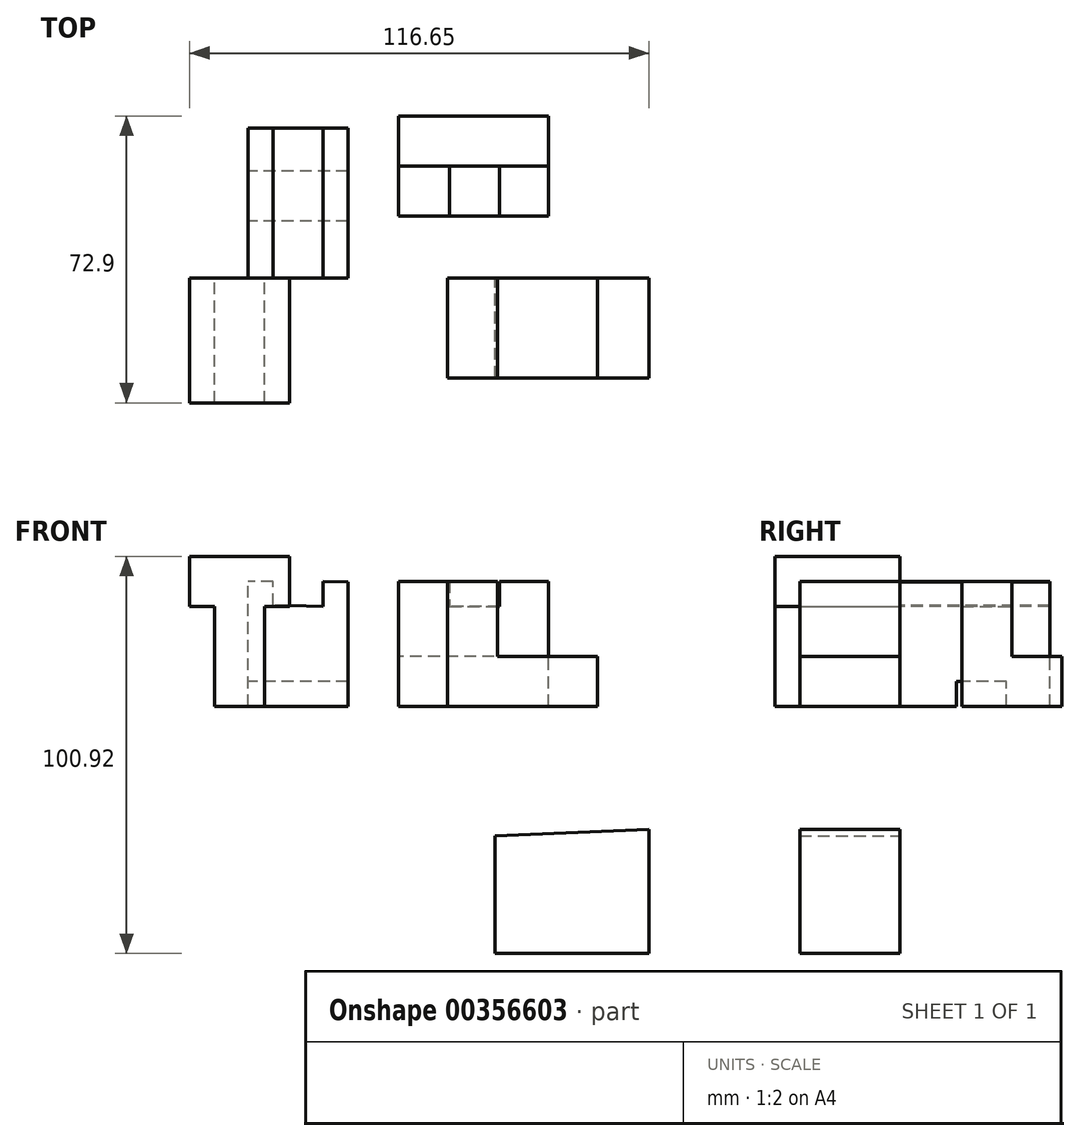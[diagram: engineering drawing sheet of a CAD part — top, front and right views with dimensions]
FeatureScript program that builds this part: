
annotation { "Feature Type Name" : "Feature", "Feature Type Description" : "" }
export const myFeature = defineFeature(function(context is Context, id is Id, definition is map)
    precondition{}
    {
        {
            var Q0;
            Q0=qCreatedBy(makeId("Front.planeOp"),FACE);
            var sketch = newSketch(context, id + "F0", { "sketchPlane" : qUnion([Q0])});
            skLineSegment(sketch, "E0", {"start": v(12.43, 31.75) * mm, "end": v(12.43, 0) * mm});
            skLineSegment(sketch, "E1", {"start": v(12.43, 0) * mm, "end": v(50.53, 0) * mm});
            skLineSegment(sketch, "E2", {"start": v(50.53, 0) * mm, "end": v(50.53, 12.7) * mm});
            skLineSegment(sketch, "E3", {"start": v(50.53, 12.7) * mm, "end": v(25.13, 12.7) * mm});
            skLineSegment(sketch, "E4", {"start": v(25.13, 12.7) * mm, "end": v(25.13, 31.75) * mm});
            skLineSegment(sketch, "E5", {"start": v(25.13, 31.75) * mm, "end": v(12.43, 31.75) * mm});
            skSolve(sketch);
        }
        {
            var Q0;
            Q0 = qSketchRegion(id + "F0", true);
            extrude(context, id + "F1", {"entities" : qUnion([Q0]), "depth" : 25.4 * mm});
        }
        {
            var Q0;
            Q0=qCreatedBy(makeId("Front.planeOp"),FACE);
            var sketch = newSketch(context, id + "F2", { "sketchPlane" : qUnion([Q0])});
            skLineSegment(sketch, "E6", {"start": v(-53.06, 38.1) * mm, "end": v(-53.06, 25.4) * mm});
            skLineSegment(sketch, "E7", {"start": v(-53.06, 25.4) * mm, "end": v(-46.7, 25.4) * mm});
            skLineSegment(sketch, "E8", {"start": v(-46.7, 25.4) * mm, "end": v(-46.7, 0) * mm});
            skLineSegment(sketch, "E9", {"start": v(-46.7, 0) * mm, "end": v(-34, 0) * mm});
            skLineSegment(sketch, "E10", {"start": v(-34, 0) * mm, "end": v(-34, 25.4) * mm});
            skLineSegment(sketch, "E11", {"start": v(-34, 25.4) * mm, "end": v(-27.66, 25.4) * mm});
            skLineSegment(sketch, "E12", {"start": v(-27.66, 25.4) * mm, "end": v(-27.66, 38.1) * mm});
            skLineSegment(sketch, "E13", {"start": v(-27.66, 38.1) * mm, "end": v(-53.06, 38.1) * mm});
            skSolve(sketch);
        }
        {
            var Q0;
            Q0 = qSketchRegion(id + "F2", true);
            extrude(context, id + "F3", {"entities" : qUnion([Q0]), "depth" : 31.75 * mm});
        }
        {
            var Q0;
            Q0=qCreatedBy(makeId("Right.planeOp"),FACE);
            var sketch = newSketch(context, id + "F4", { "sketchPlane" : qUnion([Q0])});
            skLineSegment(sketch, "E14", {"start": v(15.75, 0) * mm, "end": v(15.75, 31.75) * mm});
            skLineSegment(sketch, "E15", {"start": v(15.75, 31.75) * mm, "end": v(28.45, 31.75) * mm});
            skLineSegment(sketch, "E16", {"start": v(28.45, 31.75) * mm, "end": v(28.45, 12.7) * mm});
            skLineSegment(sketch, "E17", {"start": v(28.45, 12.7) * mm, "end": v(41.15, 12.7) * mm});
            skLineSegment(sketch, "E18", {"start": v(41.15, 12.7) * mm, "end": v(41.15, 0) * mm});
            skLineSegment(sketch, "E19", {"start": v(41.15, 0) * mm, "end": v(15.75, 0) * mm});
            skSolve(sketch);
        }
        {
            var Q0;
            Q0 = qSketchRegion(id + "F4", true);
            extrude(context, id + "F5", {"entities" : qUnion([Q0]), "depth" : 38.1 * mm});
        }
        {
            var Q0;
            Q0=makeQuery(id+"F5.opExtrude","SWEPT_FACE",FACE,{"disambiguationData":[OSD([sQuery(id+"F4.wireOp",EDGE,"E16")])]});
            var sketch = newSketch(context, id + "F6", { "sketchPlane" : qUnion([Q0])});
            skLineSegment(sketch, "E20", {"start": v(-25.68, 31.75) * mm, "end": v(-25.68, 25.4) * mm});
            skLineSegment(sketch, "E21", {"start": v(-25.68, 25.4) * mm, "end": v(-12.98, 25.4) * mm});
            skLineSegment(sketch, "E22", {"start": v(-12.98, 25.4) * mm, "end": v(-12.98, 31.75) * mm});
            skLineSegment(sketch, "E23", {"start": v(-25.68, 31.75) * mm, "end": v(-12.98, 31.75) * mm});
            skSolve(sketch);
        }
        {
            var Q0;
            Q0 = qSketchRegion(id + "F6", true);
            extrude(context, id + "F7", {"entities" : qUnion([Q0]), "operationType" : NewBodyOperationType.REMOVE, "oppositeDirection" : true, "depth" : 25.4 * mm});
        }
        {
            var Q0;
            Q0=qCreatedBy(makeId("Front.planeOp"),FACE);
            var sketch = newSketch(context, id + "F8", { "sketchPlane" : qUnion([Q0])});
            skLineSegment(sketch, "E24", {"start": v(-12.87, 0) * mm, "end": v(-38.27, 0) * mm});
            skLineSegment(sketch, "E25", {"start": v(-38.27, 0) * mm, "end": v(-38.27, 31.75) * mm});
            skLineSegment(sketch, "E26", {"start": v(-12.87, 0) * mm, "end": v(-12.87, 31.61) * mm});
            skLineSegment(sketch, "E27", {"start": v(-12.87, 31.61) * mm, "end": v(-19.22, 31.75) * mm});
            skLineSegment(sketch, "E28", {"start": v(-19.22, 31.75) * mm, "end": v(-19.22, 31.55) * mm});
            skLineSegment(sketch, "E29", {"start": v(-31.92, 31.75) * mm, "end": v(-31.92, 31.82) * mm});
            skLineSegment(sketch, "E30", {"start": v(-31.92, 31.75) * mm, "end": v(-38.27, 31.75) * mm});
            skLineSegment(sketch, "E31", {"start": v(-19.22, 31.75) * mm, "end": v(-19.22, 25.4) * mm});
            skLineSegment(sketch, "E32", {"start": v(-19.22, 25.4) * mm, "end": v(-31.91, 25.67) * mm});
            skLineSegment(sketch, "E33", {"start": v(-31.91, 25.67) * mm, "end": v(-31.92, 31.75) * mm});
            skSolve(sketch);
        }
        {
            var Q0;
            Q0 = qSketchRegion(id + "F8", true);
            extrude(context, id + "F9", {"entities" : qUnion([Q0]), "operationType" : NewBodyOperationType.ADD, "oppositeDirection" : true, "depth" : 38.1 * mm});
        }
        {
            var Q0;
            Q0=makeQuery(id+"F9.opExtrude","SWEPT_FACE",FACE,{"disambiguationData":[OSD([sQuery(id+"F8.wireOp",EDGE,"E25")])]});
            var sketch = newSketch(context, id + "F10", { "sketchPlane" : qUnion([Q0])});
            skLineSegment(sketch, "E34.bottom", {"start": v(-27.1, 0) * mm, "end": v(-14.4, 0) * mm});
            skLineSegment(sketch, "E34.top", {"start": v(-27.1, 6.35) * mm, "end": v(-14.4, 6.35) * mm});
            skLineSegment(sketch, "E34.left", {"start": v(-27.1, 0) * mm, "end": v(-27.1, 6.35) * mm});
            skLineSegment(sketch, "E34.right", {"start": v(-14.4, 0) * mm, "end": v(-14.4, 6.35) * mm});
            skSolve(sketch);
        }
        {
            var Q0;
            Q0 = qSketchRegion(id + "F10", true);
            extrude(context, id + "F11", {"entities" : qUnion([Q0]), "operationType" : NewBodyOperationType.REMOVE, "oppositeDirection" : true, "depth" : 25.4 * mm});
        }
        {
            var Q0;
            Q0=qCreatedBy(makeId("Front.planeOp"),FACE);
            var sketch = newSketch(context, id + "F12", { "sketchPlane" : qUnion([Q0])});
            skLineSegment(sketch, "E35", {"start": v(24.55, -32.91) * mm, "end": v(24.55, -62.82) * mm});
            skLineSegment(sketch, "E36", {"start": v(24.55, -62.82) * mm, "end": v(63.6, -62.82) * mm});
            skLineSegment(sketch, "E37", {"start": v(63.6, -62.82) * mm, "end": v(63.6, -31.23) * mm});
            skLineSegment(sketch, "E38", {"start": v(63.6, -31.23) * mm, "end": v(24.55, -32.91) * mm});
            skSolve(sketch);
        }
        {
            var Q0;
            Q0=makeQuery(id+"F12.imprint","IMPRINT",FACE,{"disambiguationData":[TD([[makeQuery(id+"F12.imprint","IMPRINT",EDGE,{"derivedFrom":sQuery(id+"F12.wireOp",EDGE,"E35")}),1.0]])]});
            extrude(context, id + "F13", {"entities" : qUnion([Q0]), "depth" : 25.4 * mm});
        }
    });
